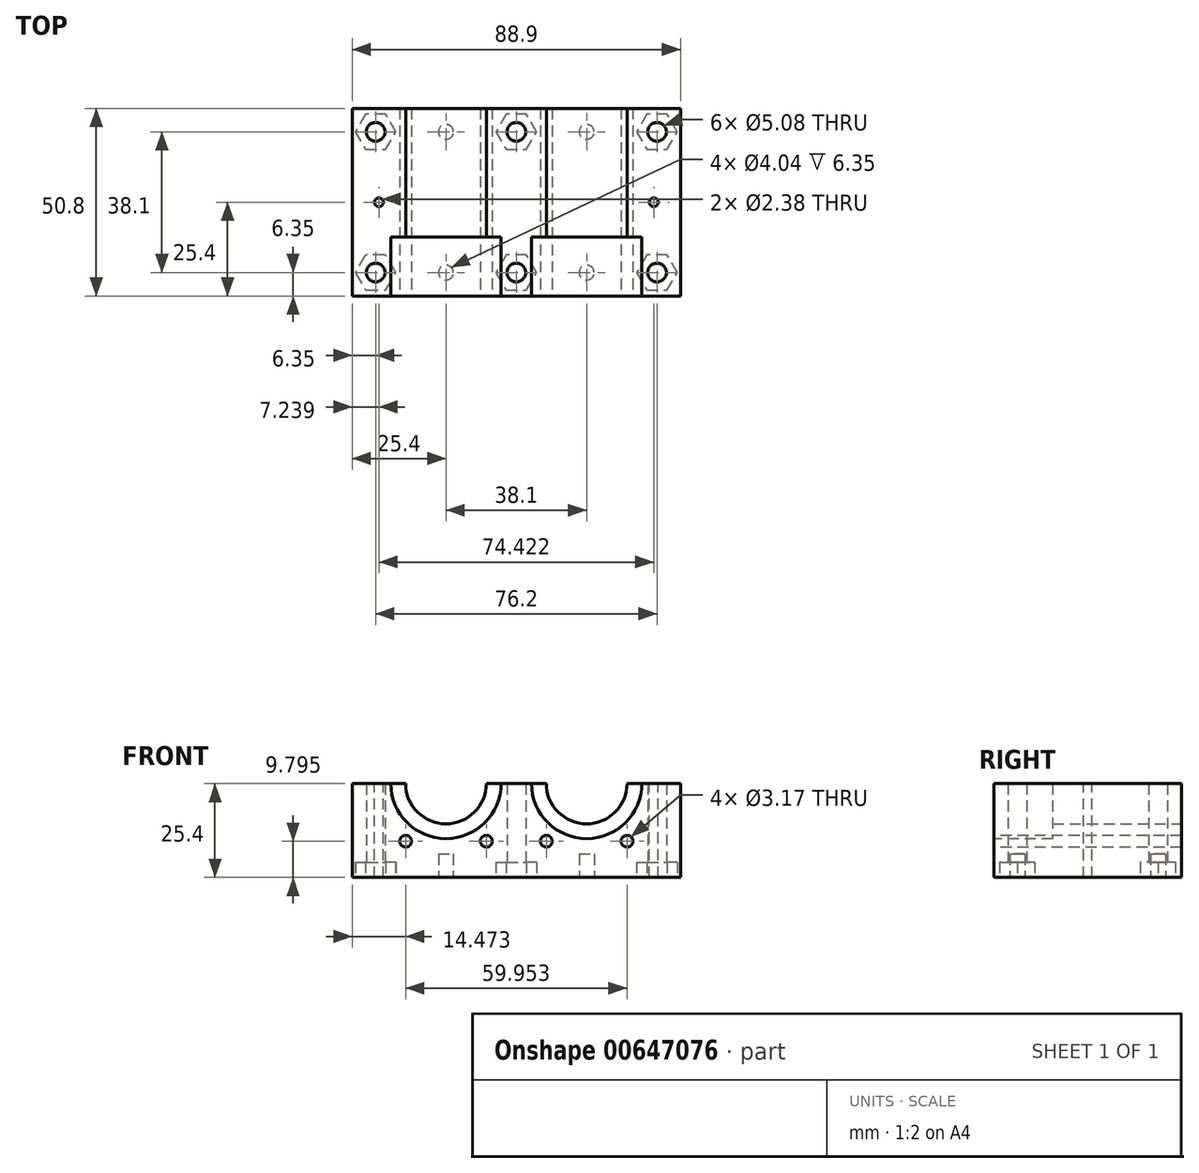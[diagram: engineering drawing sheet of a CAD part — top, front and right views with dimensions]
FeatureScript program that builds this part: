
annotation { "Feature Type Name" : "Feature", "Feature Type Description" : "" }
export const myFeature = defineFeature(function(context is Context, id is Id, definition is map)
    precondition{}
    {
        {
            var Q0;
            Q0=qCreatedBy(makeId("Front.planeOp"),FACE);
            var sketch = newSketch(context, id + "F0", { "sketchPlane" : qUnion([Q0])});
            skLineSegment(sketch, "E0.bottom", {"start": v(-44.45, 0) * mm, "end": v(-29.97, 0) * mm});
            skLineSegment(sketch, "E0.top", {"start": v(-44.45, -25.4) * mm, "end": v(44.45, -25.4) * mm});
            skLineSegment(sketch, "E0.left", {"start": v(-44.45, 0) * mm, "end": v(-44.45, -25.4) * mm});
            skLineSegment(sketch, "E0.right", {"start": v(44.45, 0) * mm, "end": v(44.45, -25.4) * mm});
            skPoint(sketch, "E1", {"position": v(0, 0) * mm});
            skArc(sketch, "E2", {"start": v(-29.97, 0) * mm, "mid": v(-19.05, -10.92) * mm, "end": v(-8.13, 0) * mm});
            skArc(sketch, "E3", {"start": v(8.13, 0) * mm, "mid": v(19.05, -10.92) * mm, "end": v(29.97, 0) * mm});
            skLineSegment(sketch, "E4.trimOffspring", {"start": v(-8.13, 0) * mm, "end": v(8.13, 0) * mm});
            skLineSegment(sketch, "E5.trimOffspring", {"start": v(29.97, 0) * mm, "end": v(44.45, 0) * mm});
            skPoint(sketch, "E6", {"position": v(-19.05, -25.4) * mm});
            skPoint(sketch, "E6.positionSnap0", {"position": v(-19.05, -10.92) * mm});
            skPoint(sketch, "E7", {"position": v(19.05, -25.4) * mm});
            skPoint(sketch, "E7.positionSnap0", {"position": v(19.05, -10.92) * mm});
            skSolve(sketch);
        }
        {
            var Q0;
            Q0 = qSketchRegion(id + "F0", true);
            extrude(context, id + "F1", {"entities" : qUnion([Q0]), "depth" : 50.8 * mm, "offsetDistance" : 25.4 * mm});
        }
        {
            var Q0;
            Q0=makeQuery(id+"F1.opExtrude","CAP_FACE",FACE,{"disambiguationData":[OSD([sQuery(id+"F0.wireOp",EDGE,"E0.bottom"),sQuery(id+"F0.wireOp",EDGE,"E0.top"),sQuery(id+"F0.wireOp",EDGE,"E0.left"),sQuery(id+"F0.wireOp",EDGE,"E0.right"),sQuery(id+"F0.wireOp",EDGE,"E2"),sQuery(id+"F0.wireOp",EDGE,"E3"),sQuery(id+"F0.wireOp",EDGE,"E4.trimOffspring"),sQuery(id+"F0.wireOp",EDGE,"E5.trimOffspring")])],"isStart":false});
            var sketch = newSketch(context, id + "F2", { "sketchPlane" : qUnion([Q0])});
            skCircle(sketch, "E8", {"center": v(-19.05, 0) * mm, "radius": 14.92 * mm});
            skCircle(sketch, "E9", {"center": v(19.05, 0) * mm, "radius": 14.92 * mm});
            skSolve(sketch);
        }
        {
            var Q0;
            Q0 = qSketchRegion(id + "F2", true);
            extrude(context, id + "F3", {"entities" : qUnion([Q0]), "operationType" : NewBodyOperationType.REMOVE, "oppositeDirection" : true, "depth" : 15.94 * mm, "offsetDistance" : 25.4 * mm});
        }
        {
            var Q0;
            Q0=makeQuery(id+"F1.opExtrude","SWEPT_FACE",FACE,{"disambiguationData":[OSD([sQuery(id+"F0.wireOp",EDGE,"E0.top")])]});
            var sketch = newSketch(context, id + "F4", { "sketchPlane" : qUnion([Q0])});
            skCircle(sketch, "E10", {"center": v(-38.1, 44.45) * mm, "radius": 2.54 * mm});
            skCircle(sketch, "E11", {"center": v(0, 44.45) * mm, "radius": 2.54 * mm});
            skCircle(sketch, "E12", {"center": v(38.1, 44.45) * mm, "radius": 2.54 * mm});
            skCircle(sketch, "E13", {"center": v(38.1, 6.35) * mm, "radius": 2.54 * mm});
            skCircle(sketch, "E14", {"center": v(0, 6.35) * mm, "radius": 2.54 * mm});
            skCircle(sketch, "E15", {"center": v(-38.1, 6.35) * mm, "radius": 2.54 * mm});
            skSolve(sketch);
        }
        {
            var Q0;
            Q0 = qSketchRegion(id + "F4", true);
            extrude(context, id + "F5", {"entities" : qUnion([Q0]), "operationType" : NewBodyOperationType.REMOVE, "endBound" : BoundingType.THROUGH_ALL, "oppositeDirection" : true, "depth" : 25.4 * mm, "offsetDistance" : 25.4 * mm});
        }
        {
            var Q0;
            Q0=makeQuery(id+"F1.opExtrude","SWEPT_FACE",FACE,{"disambiguationData":[OSD([sQuery(id+"F0.wireOp",EDGE,"E5.trimOffspring")])]});
            var sketch = newSketch(context, id + "F6", { "sketchPlane" : qUnion([Q0])});
            skPoint(sketch, "E16", {"position": v(37.21, 0) * mm});
            skPoint(sketch, "E17", {"position": v(44.45, -25.4) * mm});
            skCircle(sketch, "E18", {"center": v(37.21, -25.4) * mm, "radius": 1.2 * mm});
            skSolve(sketch);
        }
        {
            var Q0;
            Q0 = qSketchRegion(id + "F6", true);
            extrude(context, id + "F7", {"entities" : qUnion([Q0]), "operationType" : NewBodyOperationType.REMOVE, "endBound" : BoundingType.THROUGH_ALL, "oppositeDirection" : true, "depth" : 12.7 * mm, "offsetDistance" : 25.4 * mm});
        }
        {
            var Q0;
            Q0=makeQuery(id+"F1.opExtrude","SWEPT_FACE",FACE,{"disambiguationData":[OSD([sQuery(id+"F0.wireOp",EDGE,"E0.bottom")])]});
            var sketch = newSketch(context, id + "F8", { "sketchPlane" : qUnion([Q0])});
            skPoint(sketch, "E19", {"position": v(-37.21, 0) * mm});
            skPoint(sketch, "E20", {"position": v(-44.45, -25.4) * mm});
            skCircle(sketch, "E21", {"center": v(-37.21, -25.4) * mm, "radius": 1.2 * mm});
            skSolve(sketch);
        }
        {
            var Q0;
            Q0 = qSketchRegion(id + "F8", true);
            extrude(context, id + "F9", {"entities" : qUnion([Q0]), "operationType" : NewBodyOperationType.REMOVE, "endBound" : BoundingType.THROUGH_ALL, "oppositeDirection" : true, "depth" : 9.52 * mm, "offsetDistance" : 25.4 * mm});
        }
        {
            var Q0;
            Q0=makeQuery(id+"F1.opExtrude","SWEPT_FACE",FACE,{"disambiguationData":[OSD([sQuery(id+"F0.wireOp",EDGE,"E0.top")])]});
            var sketch = newSketch(context, id + "F10", { "sketchPlane" : qUnion([Q0])});
            skLineSegment(sketch, "E22", {"start": v(-32.87, 6.35) * mm, "end": v(-5.23, 6.35) * mm, "construction": true});
            skPoint(sketch, "E23", {"position": v(-19.05, 6.35) * mm});
            skCircle(sketch, "E24", {"center": v(-19.05, 6.35) * mm, "radius": 2.02 * mm});
            skLineSegment(sketch, "E25", {"start": v(-32.87, 44.45) * mm, "end": v(-5.23, 44.45) * mm, "construction": true});
            skPoint(sketch, "E26", {"position": v(-19.05, 44.45) * mm});
            skCircle(sketch, "E27", {"center": v(-19.05, 44.45) * mm, "radius": 2.02 * mm});
            skLineSegment(sketch, "E28", {"start": v(32.87, 44.45) * mm, "end": v(5.23, 44.45) * mm, "construction": true});
            skPoint(sketch, "E29", {"position": v(19.05, 44.45) * mm});
            skCircle(sketch, "E30", {"center": v(19.05, 44.45) * mm, "radius": 2.02 * mm});
            skLineSegment(sketch, "E31", {"start": v(5.23, 6.35) * mm, "end": v(32.87, 6.35) * mm, "construction": true});
            skPoint(sketch, "E32", {"position": v(19.05, 6.35) * mm});
            skCircle(sketch, "E33", {"center": v(19.05, 6.35) * mm, "radius": 2.02 * mm});
            skSolve(sketch);
        }
        {
            var Q0;
            Q0 = qSketchRegion(id + "F10", true);
            var Q1;
            Q1 = qSketchRegion(id + "F8", true);
            extrude(context, id + "F11", {"entities" : qUnion([Q0, Q1]), "operationType" : NewBodyOperationType.REMOVE, "oppositeDirection" : true, "depth" : 6.35 * mm, "offsetDistance" : 25.4 * mm});
        }
        {
            var Q0;
            Q0=makeQuery(id+"F1.opExtrude","SWEPT_FACE",FACE,{"disambiguationData":[OSD([sQuery(id+"F0.wireOp",EDGE,"E0.top")])]});
            var sketch = newSketch(context, id + "F12", { "sketchPlane" : qUnion([Q0])});
            skCircle(sketch, "E34.cCircle", {"center": v(-38.1, 44.45) * mm, "radius": 4.76 * mm, "construction": true});
            skLineSegment(sketch, "E34.0", {"start": v(-40.4, 49.21) * mm, "end": v(-35.8, 49.21) * mm});
            skLineSegment(sketch, "E34.1", {"start": v(-35.12, 48.82) * mm, "end": v(-32.83, 44.85) * mm});
            skLineSegment(sketch, "E34.2", {"start": v(-32.83, 44.05) * mm, "end": v(-35.12, 40.08) * mm});
            skLineSegment(sketch, "E34.3", {"start": v(-35.8, 39.69) * mm, "end": v(-40.4, 39.69) * mm});
            skLineSegment(sketch, "E34.4", {"start": v(-41.08, 40.08) * mm, "end": v(-43.37, 44.05) * mm});
            skLineSegment(sketch, "E34.5", {"start": v(-43.37, 44.85) * mm, "end": v(-41.08, 48.82) * mm});
            skPoint(sketch, "E34.0.midPoint", {"position": v(-38.1, 49.21) * mm});
            skCircle(sketch, "E35.cCircle", {"center": v(0, 44.45) * mm, "radius": 4.76 * mm, "construction": true});
            skLineSegment(sketch, "E35.0", {"start": v(-2.75, 49.21) * mm, "end": v(2.75, 49.21) * mm});
            skLineSegment(sketch, "E35.1", {"start": v(2.75, 49.21) * mm, "end": v(5.5, 44.45) * mm});
            skLineSegment(sketch, "E35.2", {"start": v(5.5, 44.45) * mm, "end": v(2.75, 39.69) * mm});
            skLineSegment(sketch, "E35.3", {"start": v(2.75, 39.69) * mm, "end": v(-2.75, 39.69) * mm});
            skLineSegment(sketch, "E35.4", {"start": v(-2.75, 39.69) * mm, "end": v(-5.5, 44.45) * mm});
            skLineSegment(sketch, "E35.5", {"start": v(-5.5, 44.45) * mm, "end": v(-2.75, 49.21) * mm});
            skPoint(sketch, "E35.0.midPoint", {"position": v(0, 49.21) * mm});
            skCircle(sketch, "E36.cCircle", {"center": v(38.1, 44.45) * mm, "radius": 4.76 * mm, "construction": true});
            skLineSegment(sketch, "E36.0", {"start": v(35.35, 49.21) * mm, "end": v(40.85, 49.21) * mm});
            skLineSegment(sketch, "E36.1", {"start": v(40.85, 49.21) * mm, "end": v(43.6, 44.45) * mm});
            skLineSegment(sketch, "E36.2", {"start": v(43.6, 44.45) * mm, "end": v(40.85, 39.69) * mm});
            skLineSegment(sketch, "E36.3", {"start": v(40.85, 39.69) * mm, "end": v(35.35, 39.69) * mm});
            skLineSegment(sketch, "E36.4", {"start": v(35.35, 39.69) * mm, "end": v(32.6, 44.45) * mm});
            skLineSegment(sketch, "E36.5", {"start": v(32.6, 44.45) * mm, "end": v(35.35, 49.21) * mm});
            skPoint(sketch, "E36.0.midPoint", {"position": v(38.1, 49.21) * mm});
            skCircle(sketch, "E37.cCircle", {"center": v(38.1, 6.35) * mm, "radius": 4.76 * mm, "construction": true});
            skLineSegment(sketch, "E37.0", {"start": v(35.35, 11.11) * mm, "end": v(40.85, 11.11) * mm});
            skLineSegment(sketch, "E37.1", {"start": v(40.85, 11.11) * mm, "end": v(43.6, 6.35) * mm});
            skLineSegment(sketch, "E37.2", {"start": v(43.6, 6.35) * mm, "end": v(40.85, 1.59) * mm});
            skLineSegment(sketch, "E37.3", {"start": v(40.85, 1.59) * mm, "end": v(35.35, 1.59) * mm});
            skLineSegment(sketch, "E37.4", {"start": v(35.35, 1.59) * mm, "end": v(32.6, 6.35) * mm});
            skLineSegment(sketch, "E37.5", {"start": v(32.6, 6.35) * mm, "end": v(35.35, 11.11) * mm});
            skPoint(sketch, "E37.0.midPoint", {"position": v(38.1, 11.11) * mm});
            skCircle(sketch, "E38.cCircle", {"center": v(0, 6.35) * mm, "radius": 4.76 * mm, "construction": true});
            skLineSegment(sketch, "E38.0", {"start": v(-2.75, 11.11) * mm, "end": v(2.75, 11.11) * mm});
            skLineSegment(sketch, "E38.1", {"start": v(2.75, 11.11) * mm, "end": v(5.5, 6.35) * mm});
            skLineSegment(sketch, "E38.2", {"start": v(5.5, 6.35) * mm, "end": v(2.75, 1.59) * mm});
            skLineSegment(sketch, "E38.3", {"start": v(2.75, 1.59) * mm, "end": v(-2.75, 1.59) * mm});
            skLineSegment(sketch, "E38.4", {"start": v(-2.75, 1.59) * mm, "end": v(-5.5, 6.35) * mm});
            skLineSegment(sketch, "E38.5", {"start": v(-5.5, 6.35) * mm, "end": v(-2.75, 11.11) * mm});
            skPoint(sketch, "E38.0.midPoint", {"position": v(0, 11.11) * mm});
            skCircle(sketch, "E39.cCircle", {"center": v(-38.1, 6.35) * mm, "radius": 4.76 * mm, "construction": true});
            skLineSegment(sketch, "E39.0", {"start": v(-40.85, 11.11) * mm, "end": v(-35.35, 11.11) * mm});
            skLineSegment(sketch, "E39.1", {"start": v(-35.35, 11.11) * mm, "end": v(-32.6, 6.35) * mm});
            skLineSegment(sketch, "E39.2", {"start": v(-32.6, 6.35) * mm, "end": v(-35.35, 1.59) * mm});
            skLineSegment(sketch, "E39.3", {"start": v(-35.35, 1.59) * mm, "end": v(-40.85, 1.59) * mm});
            skLineSegment(sketch, "E39.4", {"start": v(-40.85, 1.59) * mm, "end": v(-43.6, 6.35) * mm});
            skLineSegment(sketch, "E39.5", {"start": v(-43.6, 6.35) * mm, "end": v(-40.85, 11.11) * mm});
            skPoint(sketch, "E39.0.midPoint", {"position": v(-38.1, 11.11) * mm});
            skPoint(sketch, "E40.visualSharp", {"position": v(-40.85, 49.21) * mm});
            skArc(sketch, "E40.filletArc", {"start": v(-40.4, 49.21) * mm, "mid": v(-40.79, 49.1) * mm, "end": v(-41.08, 48.82) * mm});
            skPoint(sketch, "E41.visualSharp", {"position": v(-35.35, 49.21) * mm});
            skArc(sketch, "E41.filletArc", {"start": v(-35.12, 48.82) * mm, "mid": v(-35.41, 49.1) * mm, "end": v(-35.8, 49.21) * mm});
            skPoint(sketch, "E42.visualSharp", {"position": v(-32.6, 44.45) * mm});
            skArc(sketch, "E42.filletArc", {"start": v(-32.83, 44.05) * mm, "mid": v(-32.72, 44.45) * mm, "end": v(-32.83, 44.85) * mm});
            skPoint(sketch, "E43.visualSharp", {"position": v(-35.35, 39.69) * mm});
            skArc(sketch, "E43.filletArc", {"start": v(-35.8, 39.69) * mm, "mid": v(-35.41, 39.8) * mm, "end": v(-35.12, 40.08) * mm});
            skPoint(sketch, "E44.visualSharp", {"position": v(-40.85, 39.69) * mm});
            skArc(sketch, "E44.filletArc", {"start": v(-41.08, 40.08) * mm, "mid": v(-40.79, 39.8) * mm, "end": v(-40.4, 39.69) * mm});
            skPoint(sketch, "E45.visualSharp", {"position": v(-43.6, 44.45) * mm});
            skArc(sketch, "E45.filletArc", {"start": v(-43.37, 44.85) * mm, "mid": v(-43.48, 44.45) * mm, "end": v(-43.37, 44.05) * mm});
            skSolve(sketch);
        }
        {
            var Q0;
            Q0 = qSketchRegion(id + "F12", true);
            extrude(context, id + "F13", {"entities" : qUnion([Q0]), "operationType" : NewBodyOperationType.REMOVE, "oppositeDirection" : true, "depth" : 4.13 * mm, "offsetDistance" : 25.4 * mm});
        }
        {
            var Q0;
            Q0=makeQuery(id+"F1.opExtrude","CAP_FACE",FACE,{"disambiguationData":[OSD([sQuery(id+"F0.wireOp",EDGE,"E0.bottom"),sQuery(id+"F0.wireOp",EDGE,"E0.top"),sQuery(id+"F0.wireOp",EDGE,"E0.left"),sQuery(id+"F0.wireOp",EDGE,"E0.right"),sQuery(id+"F0.wireOp",EDGE,"E2"),sQuery(id+"F0.wireOp",EDGE,"E3"),sQuery(id+"F0.wireOp",EDGE,"E4.trimOffspring"),sQuery(id+"F0.wireOp",EDGE,"E5.trimOffspring")])],"isStart":false});
            var sketch = newSketch(context, id + "F14", { "sketchPlane" : qUnion([Q0])});
            skPoint(sketch, "E46", {"position": v(19.05, 0) * mm});
            skPoint(sketch, "E47", {"position": v(-19.05, 0) * mm});
            skLineSegment(sketch, "E48", {"start": v(19.05, 0) * mm, "end": v(29.98, -15.6) * mm, "construction": true});
            skLineSegment(sketch, "E49", {"start": v(19.05, 0) * mm, "end": v(8.12, -15.6) * mm, "construction": true});
            skCircle(sketch, "E50", {"center": v(29.98, -15.6) * mm, "radius": 1.59 * mm});
            skCircle(sketch, "E51", {"center": v(8.12, -15.6) * mm, "radius": 1.59 * mm});
            skLineSegment(sketch, "E52", {"start": v(-19.05, 0) * mm, "end": v(-8.12, -15.6) * mm, "construction": true});
            skLineSegment(sketch, "E53", {"start": v(-19.05, 0) * mm, "end": v(-29.98, -15.6) * mm, "construction": true});
            skCircle(sketch, "E54", {"center": v(-8.12, -15.6) * mm, "radius": 1.59 * mm});
            skCircle(sketch, "E55", {"center": v(-29.98, -15.6) * mm, "radius": 1.59 * mm});
            skSolve(sketch);
        }
        {
            var Q0;
            Q0 = qSketchRegion(id + "F14", true);
            extrude(context, id + "F15", {"entities" : qUnion([Q0]), "operationType" : NewBodyOperationType.REMOVE, "endBound" : BoundingType.THROUGH_ALL, "oppositeDirection" : true, "depth" : 25.4 * mm, "offsetDistance" : 25.4 * mm});
        }
    });
